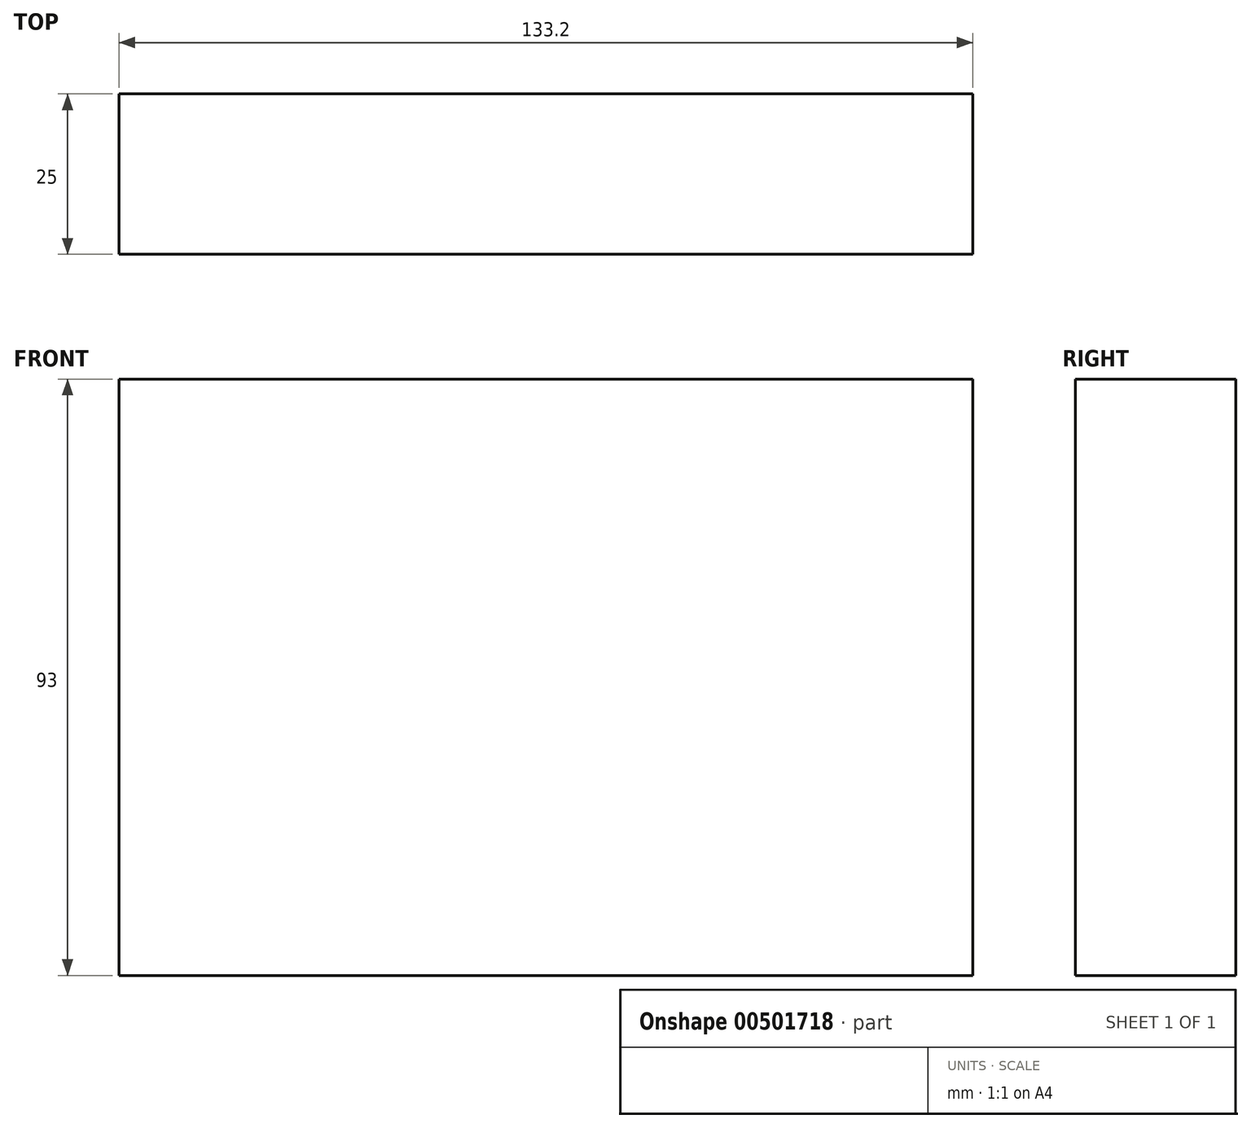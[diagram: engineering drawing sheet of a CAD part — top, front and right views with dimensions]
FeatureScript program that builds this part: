
annotation { "Feature Type Name" : "Feature", "Feature Type Description" : "" }
export const myFeature = defineFeature(function(context is Context, id is Id, definition is map)
    precondition{}
    {
        {
            var Q0;
            Q0=qCreatedBy(makeId("Front.planeOp"),FACE);
            var sketch = newSketch(context, id + "F0", { "sketchPlane" : qUnion([Q0])});
            skLineSegment(sketch, "E0.bottom", {"start": v(-75.6, 55.05) * mm, "end": v(75.3, 55.05) * mm});
            skLineSegment(sketch, "E0.top", {"start": v(-75.6, -55.35) * mm, "end": v(75.3, -55.35) * mm});
            skLineSegment(sketch, "E0.left", {"start": v(-75.6, 55.05) * mm, "end": v(-75.6, -55.35) * mm});
            skLineSegment(sketch, "E0.right", {"start": v(75.3, 55.05) * mm, "end": v(75.3, -55.35) * mm});
            skSolve(sketch);
        }
        {
            var Q0;
            Q0=makeQuery(id+"F0.imprint","IMPRINT",FACE,{"disambiguationData":[TD([[makeQuery(id+"F0.imprint","IMPRINT",EDGE,{"derivedFrom":sQuery(id+"F0.wireOp",EDGE,"E0.bottom")}),-1.0]])]});
            var sketch = newSketch(context, id + "F1", { "sketchPlane" : qUnion([Q0])});
            skLineSegment(sketch, "E1.bottom", {"start": v(-67.35, 47.55) * mm, "end": v(65.85, 47.55) * mm});
            skLineSegment(sketch, "E1.top", {"start": v(-67.35, -45.45) * mm, "end": v(65.85, -45.45) * mm});
            skLineSegment(sketch, "E1.left", {"start": v(-67.35, 47.55) * mm, "end": v(-67.35, -45.45) * mm});
            skLineSegment(sketch, "E1.right", {"start": v(65.85, 47.55) * mm, "end": v(65.85, -45.45) * mm});
            skSolve(sketch);
        }
        {
            var Q0;
            Q0=makeQuery(id+"F1.imprint","IMPRINT",FACE,{"disambiguationData":[TD([[makeQuery(id+"F1.imprint","IMPRINT",EDGE,{"derivedFrom":sQuery(id+"F1.wireOp",EDGE,"E1.bottom")}),-1.0]])]});
            extrude(context, id + "F2", {"entities" : qUnion([Q0]), "depth" : 25 * mm, "offsetDistance" : 25 * mm});
        }
    });
